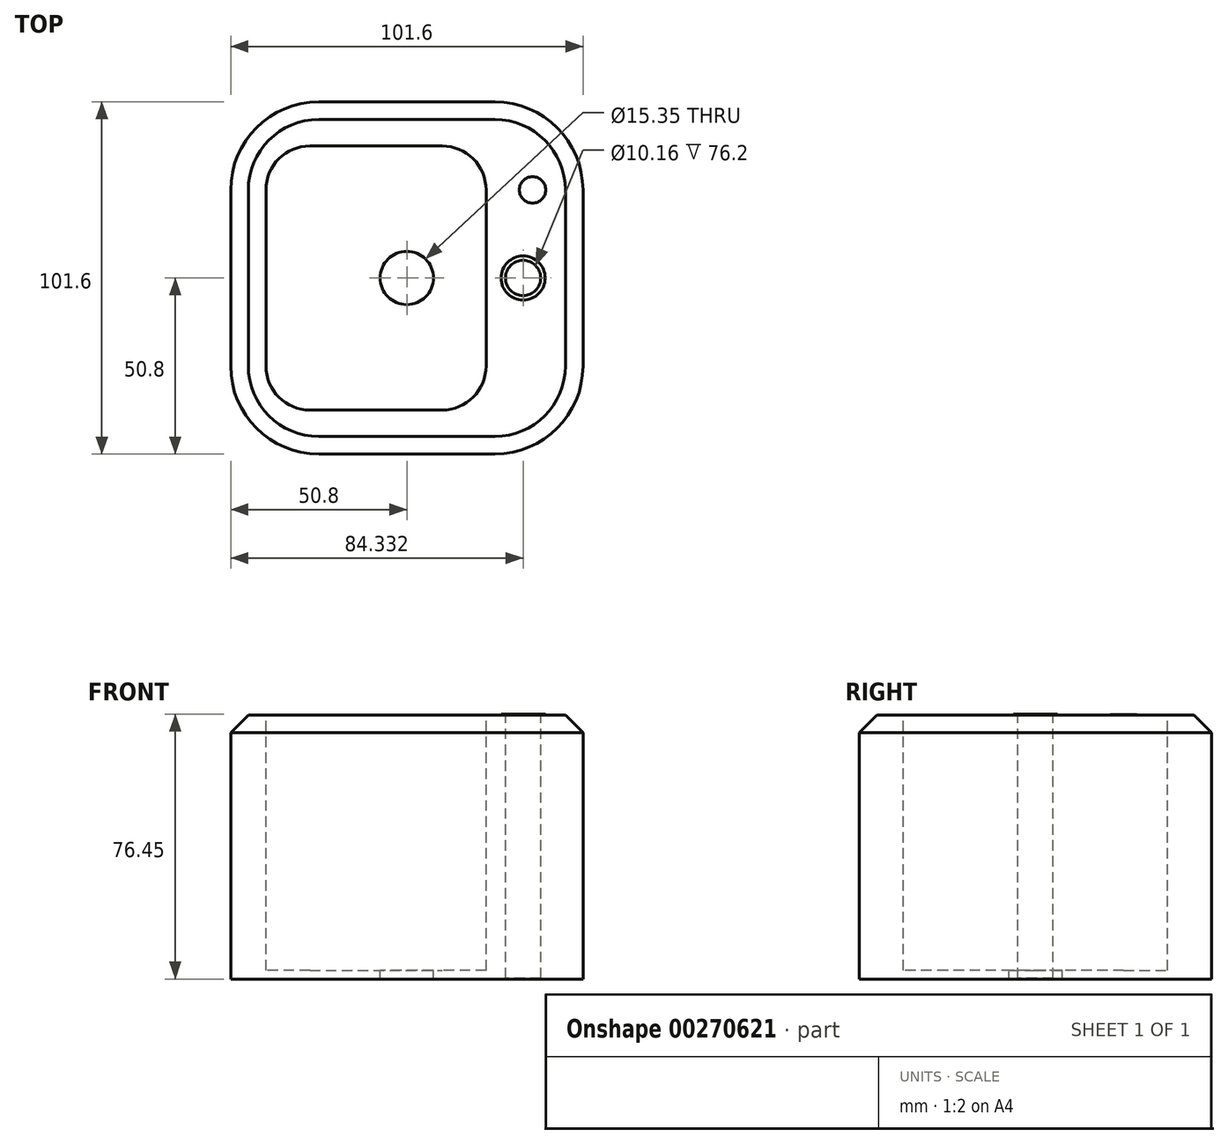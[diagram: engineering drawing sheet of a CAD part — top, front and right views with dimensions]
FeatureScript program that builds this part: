
annotation { "Feature Type Name" : "Feature", "Feature Type Description" : "" }
export const myFeature = defineFeature(function(context is Context, id is Id, definition is map)
    precondition{}
    {
        {
            var Q0;
            Q0=qCreatedBy(makeId("Top.planeOp"),FACE);
            var sketch = newSketch(context, id + "F0", { "sketchPlane" : qUnion([Q0])});
            skLineSegment(sketch, "E0.bottom", {"start": v(50.8, 50.8) * mm, "end": v(-50.8, 50.8) * mm});
            skLineSegment(sketch, "E0.top", {"start": v(50.8, -50.8) * mm, "end": v(-50.8, -50.8) * mm});
            skLineSegment(sketch, "E0.left", {"start": v(50.8, 50.8) * mm, "end": v(50.8, -50.8) * mm});
            skLineSegment(sketch, "E0.right", {"start": v(-50.8, 50.8) * mm, "end": v(-50.8, -50.8) * mm});
            skPoint(sketch, "E0.middle", {"position": v(0, 0) * mm});
            skSolve(sketch);
        }
        {
            var Q0;
            Q0=makeQuery(id+"F0.imprint","IMPRINT",FACE,{"disambiguationData":[TD([[makeQuery(id+"F0.imprint","IMPRINT",EDGE,{"derivedFrom":sQuery(id+"F0.wireOp",EDGE,"E0.bottom")}),1.0]])]});
            extrude(context, id + "F1", {"entities" : qUnion([Q0]), "depth" : 76.2 * mm});
        }
        {
            var Q0;
            Q0=makeQuery(id+"F1.opExtrude","CAP_FACE",FACE,{"disambiguationData":[OSD([sQuery(id+"F0.wireOp",EDGE,"E0.bottom"),sQuery(id+"F0.wireOp",EDGE,"E0.top"),sQuery(id+"F0.wireOp",EDGE,"E0.left"),sQuery(id+"F0.wireOp",EDGE,"E0.right")])],"isStart":false});
            var sketch = newSketch(context, id + "F2", { "sketchPlane" : qUnion([Q0])});
            skLineSegment(sketch, "E1.bottom", {"start": v(-27.94, 38.1) * mm, "end": v(10.16, 38.1) * mm});
            skLineSegment(sketch, "E1.top", {"start": v(-27.94, -38.1) * mm, "end": v(10.16, -38.1) * mm});
            skLineSegment(sketch, "E1.left", {"start": v(-40.64, 25.4) * mm, "end": v(-40.64, -25.4) * mm});
            skLineSegment(sketch, "E1.right", {"start": v(22.86, 25.4) * mm, "end": v(22.86, -25.4) * mm});
            skPoint(sketch, "E2.visualSharp", {"position": v(-40.64, 38.1) * mm});
            skArc(sketch, "E2.filletArc", {"start": v(-27.94, 38.1) * mm, "mid": v(-36.92, 34.38) * mm, "end": v(-40.64, 25.4) * mm});
            skPoint(sketch, "E3.visualSharp", {"position": v(22.86, 38.1) * mm});
            skArc(sketch, "E3.filletArc", {"start": v(22.86, 25.4) * mm, "mid": v(19.14, 34.38) * mm, "end": v(10.16, 38.1) * mm});
            skPoint(sketch, "E4.visualSharp", {"position": v(22.86, -38.1) * mm});
            skArc(sketch, "E4.filletArc", {"start": v(10.16, -38.1) * mm, "mid": v(19.14, -34.38) * mm, "end": v(22.86, -25.4) * mm});
            skPoint(sketch, "E5.visualSharp", {"position": v(-40.64, -38.1) * mm});
            skArc(sketch, "E5.filletArc", {"start": v(-40.64, -25.4) * mm, "mid": v(-36.92, -34.38) * mm, "end": v(-27.94, -38.1) * mm});
            skSolve(sketch);
        }
        {
            var Q0;
            Q0=makeQuery(id+"F1.opExtrude","SWEPT_EDGE",EDGE,{"disambiguationData":[OSD([sQuery(id+"F0.wireOp",EDGE,"E0.bottom"),sQuery(id+"F0.wireOp",EDGE,"E0.right")])]});
            var Q1;
            Q1=makeQuery(id+"F1.opExtrude","SWEPT_EDGE",EDGE,{"disambiguationData":[OSD([sQuery(id+"F0.wireOp",EDGE,"E0.bottom"),sQuery(id+"F0.wireOp",EDGE,"E0.left")])]});
            var Q2;
            Q2=makeQuery(id+"F1.opExtrude","SWEPT_EDGE",EDGE,{"disambiguationData":[OSD([sQuery(id+"F0.wireOp",EDGE,"E0.top"),sQuery(id+"F0.wireOp",EDGE,"E0.left")])]});
            var Q3;
            Q3=makeQuery(id+"F1.opExtrude","SWEPT_EDGE",EDGE,{"disambiguationData":[OSD([sQuery(id+"F0.wireOp",EDGE,"E0.top"),sQuery(id+"F0.wireOp",EDGE,"E0.right")])]});
            fillet(context, id + "F3", {"entities" : qUnion([Q0, Q1, Q2, Q3]), "radius" : 25.4 * mm, "tangentPropagation" : true, "allowEdgeOverflow" : false});
        }
        {
            var Q0;
            Q0=makeQuery(id+"F1.opExtrude","CAP_EDGE",EDGE,{"disambiguationData":[OSD([sQuery(id+"F0.wireOp",EDGE,"E0.right")])],"isStart":false});
            chamfer(context, id + "F4", {"entities" : qUnion([Q0]), "width" : 5.08 * mm, "tangentPropagation" : true});
        }
        {
            var Q0;
            Q0=makeQuery(id+"F2.imprint","IMPRINT",FACE,{"disambiguationData":[TD([[makeQuery(id+"F2.imprint","IMPRINT",EDGE,{"derivedFrom":sQuery(id+"F2.wireOp",EDGE,"E1.bottom")}),-1.0]])]});
            extrude(context, id + "F5", {"entities" : qUnion([Q0]), "operationType" : NewBodyOperationType.REMOVE, "oppositeDirection" : true, "depth" : 73.66 * mm});
        }
        {
            var Q0;
            Q0=makeQuery(id+"F5.boolean.opBoolean","COPY",FACE,{"derivedFrom":makeQuery(id+"F5.opExtrude","CAP_FACE",FACE,{"disambiguationData":[OSD([sQuery(id+"F2.wireOp",EDGE,"E1.bottom"),sQuery(id+"F2.wireOp",EDGE,"E1.top"),sQuery(id+"F2.wireOp",EDGE,"E1.left"),sQuery(id+"F2.wireOp",EDGE,"E1.right"),sQuery(id+"F2.wireOp",EDGE,"E2.filletArc"),sQuery(id+"F2.wireOp",EDGE,"E3.filletArc"),sQuery(id+"F2.wireOp",EDGE,"E4.filletArc"),sQuery(id+"F2.wireOp",EDGE,"E5.filletArc")])],"isStart":false})});
            var sketch = newSketch(context, id + "F6", { "sketchPlane" : qUnion([Q0])});
            skCircle(sketch, "E6", {"center": v(0, 0) * mm, "radius": 7.68 * mm});
            skSolve(sketch);
        }
        {
            var Q0;
            Q0=makeQuery(id+"F6.imprint","IMPRINT",FACE,{"disambiguationData":[TD([[makeQuery(id+"F6.imprint","IMPRINT",EDGE,{"derivedFrom":sQuery(id+"F6.wireOp",EDGE,"E6")}),1.0]])]});
            extrude(context, id + "F7", {"entities" : qUnion([Q0]), "operationType" : NewBodyOperationType.REMOVE, "oppositeDirection" : true, "depth" : 25.4 * mm});
        }
        {
            var Q0;
            Q0=makeQuery(id+"F1.opExtrude","CAP_FACE",FACE,{"disambiguationData":[OSD([sQuery(id+"F0.wireOp",EDGE,"E0.bottom"),sQuery(id+"F0.wireOp",EDGE,"E0.top"),sQuery(id+"F0.wireOp",EDGE,"E0.left"),sQuery(id+"F0.wireOp",EDGE,"E0.right")])],"isStart":false});
            var sketch = newSketch(context, id + "F8", { "sketchPlane" : qUnion([Q0])});
            skCircle(sketch, "E7", {"center": v(33.53, 0) * mm, "radius": 6.35 * mm});
            skSolve(sketch);
        }
        {
            var Q0;
            Q0=makeQuery(id+"F8.imprint","IMPRINT",FACE,{"disambiguationData":[TD([[makeQuery(id+"F8.imprint","IMPRINT",EDGE,{"derivedFrom":sQuery(id+"F8.wireOp",EDGE,"E7")}),1.0]])]});
            extrude(context, id + "F9", {"entities" : qUnion([Q0]), "operationType" : NewBodyOperationType.ADD, "depth" : 0.25 * mm});
        }
        {
            var Q0;
            Q0=makeQuery(id+"F9.opExtrude","CAP_FACE",FACE,{"disambiguationData":[OSD([sQuery(id+"F8.wireOp",EDGE,"E7")])],"isStart":false});
            var sketch = newSketch(context, id + "F10", { "sketchPlane" : qUnion([Q0])});
            skCircle(sketch, "E8", {"center": v(33.53, 0) * mm, "radius": 5.08 * mm});
            skSolve(sketch);
        }
        {
            var Q0;
            Q0=makeQuery(id+"F10.imprint","IMPRINT",FACE,{"disambiguationData":[TD([[makeQuery(id+"F10.imprint","IMPRINT",EDGE,{"derivedFrom":sQuery(id+"F10.wireOp",EDGE,"E8")}),1.0]])]});
            extrude(context, id + "F11", {"entities" : qUnion([Q0]), "operationType" : NewBodyOperationType.REMOVE, "oppositeDirection" : true, "depth" : 76.2 * mm});
        }
        {
            var Q0;
            Q0=makeQuery(id+"F1.opExtrude","CAP_FACE",FACE,{"disambiguationData":[OSD([sQuery(id+"F0.wireOp",EDGE,"E0.bottom"),sQuery(id+"F0.wireOp",EDGE,"E0.top"),sQuery(id+"F0.wireOp",EDGE,"E0.left"),sQuery(id+"F0.wireOp",EDGE,"E0.right")])],"isStart":false});
            var sketch = newSketch(context, id + "F12", { "sketchPlane" : qUnion([Q0])});
            skCircle(sketch, "E9", {"center": v(36.26, 25.4) * mm, "radius": 3.81 * mm});
            skSolve(sketch);
        }
        {
            var Q0;
            Q0=makeQuery(id+"F12.imprint","IMPRINT",FACE,{"disambiguationData":[TD([[makeQuery(id+"F12.imprint","IMPRINT",EDGE,{"derivedFrom":sQuery(id+"F12.wireOp",EDGE,"E9")}),1.0]])]});
            extrude(context, id + "F13", {"entities" : qUnion([Q0]), "operationType" : NewBodyOperationType.ADD, "depth" : 0.03 * mm});
        }
    });
